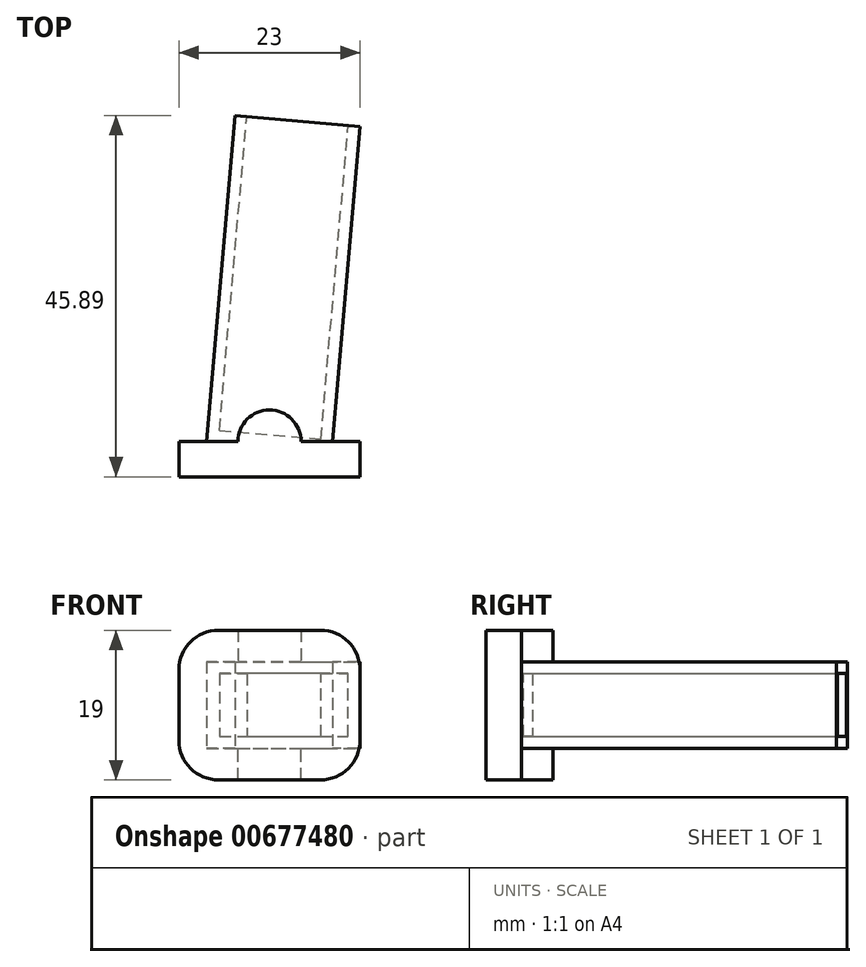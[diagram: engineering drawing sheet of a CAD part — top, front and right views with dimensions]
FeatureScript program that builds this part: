
annotation { "Feature Type Name" : "Feature", "Feature Type Description" : "" }
export const myFeature = defineFeature(function(context is Context, id is Id, definition is map)
    precondition{}
    {
        {
            var Q0;
            Q0=qCreatedBy(makeId("Top.planeOp"),FACE);
            var sketch = newSketch(context, id + "F0", { "sketchPlane" : qUnion([Q0])});
            skLineSegment(sketch, "E0", {"start": v(29.52, -9.85) * mm, "end": v(25.9, -51.24) * mm});
            skLineSegment(sketch, "E1", {"start": v(29.52, -9.85) * mm, "end": v(45.4, -11.24) * mm});
            skLineSegment(sketch, "E2", {"start": v(45.4, -11.24) * mm, "end": v(41.9, -51.24) * mm});
            skLineSegment(sketch, "E3", {"start": v(25.9, -51.24) * mm, "end": v(41.9, -51.24) * mm});
            skLineSegment(sketch, "E4", {"start": v(25.9, -51.24) * mm, "end": v(22.4, -51.24) * mm});
            skLineSegment(sketch, "E5", {"start": v(22.4, -51.24) * mm, "end": v(22.4, -55.74) * mm});
            skLineSegment(sketch, "E6", {"start": v(22.4, -55.74) * mm, "end": v(45.4, -55.74) * mm});
            skLineSegment(sketch, "E7", {"start": v(41.9, -51.24) * mm, "end": v(45.4, -51.24) * mm});
            skLineSegment(sketch, "E8", {"start": v(45.4, -51.24) * mm, "end": v(45.4, -55.74) * mm});
            skSolve(sketch);
        }
        {
            var Q0;
            {var subQ0=sQuery(id+"F0.wireOp",EDGE,"E2");Q0=makeQuery(id+"F0.imprint","IMPRINT",FACE,{"disambiguationData":[TD([[makeQuery(id+"F0.imprint","IMPRINT",EDGE,{"derivedFrom":subQ0}),-1.0]])]});}
            extrude(context, id + "F1", {"entities" : qUnion([Q0]), "endBound" : BoundingType.SYMMETRIC, "depth" : 11 * mm, "offsetDistance" : 25 * mm});
        }
        {
            var Q0;
            Q0=makeQuery(id+"F0.imprint","IMPRINT",FACE,{"disambiguationData":[TD([[makeQuery(id+"F0.imprint","IMPRINT",EDGE,{"derivedFrom":sQuery(id+"F0.wireOp",EDGE,"E3")}),-1.0]])]});
            var Q1;
            Q1=qSketchRegion(id+"F0e6qLEDJKoxhYJ_1",true);
            extrude(context, id + "F2", {"entities" : qUnion([Q0, Q1]), "operationType" : NewBodyOperationType.ADD, "endBound" : BoundingType.SYMMETRIC, "depth" : 19 * mm, "offsetDistance" : 25 * mm});
        }
        {
            var Q0;
            Q0=makeQuery(id+"F1.opExtrude","SWEPT_FACE",FACE,{"disambiguationData":[OSD([sQuery(id+"F0.wireOp",EDGE,"E1")])]});
            var sketch = newSketch(context, id + "F3", { "sketchPlane" : qUnion([Q0])});
            skLineSegment(sketch, "E9", {"start": v(-31.77, -4) * mm, "end": v(-44.7, -4) * mm});
            skLineSegment(sketch, "E10", {"start": v(-44.7, -4) * mm, "end": v(-44.7, 4) * mm});
            skLineSegment(sketch, "E11", {"start": v(-44.7, 4) * mm, "end": v(-31.77, 4) * mm});
            skLineSegment(sketch, "E12", {"start": v(-31.77, 4) * mm, "end": v(-31.77, -4) * mm});
            skSolve(sketch);
        }
        {
            var Q0;
            Q0=makeQuery(id+"F1.opExtrude","CAP_FACE",FACE,{"disambiguationData":[OSD([sQuery(id+"F0.wireOp",EDGE,"E0"),sQuery(id+"F0.wireOp",EDGE,"E1"),sQuery(id+"F0.wireOp",EDGE,"E2"),sQuery(id+"F0.wireOp",EDGE,"E3")])],"isStart":false});
            var sketch = newSketch(context, id + "F4", { "sketchPlane" : qUnion([Q0])});
            skCircle(sketch, "E13", {"center": v(33.9, -51.24) * mm, "radius": 4 * mm});
            skSolve(sketch);
        }
        {
            var Q0;
            {var subQ0=sQuery(id+"F4.wireOp",EDGE,"E13");var subQ1=makeQuery(id+"F1.opExtrude","CAP_EDGE",EDGE,{"disambiguationData":[OSD([sQuery(id+"F0.wireOp",EDGE,"E3")])],"isStart":false});var subQ2=makeQuery(id+"F4.imprint","INTERSECT",VERTEX,{"disambiguationData":[OD(0.0)],"derivedFrom":[subQ1,subQ0]});Q0=makeQuery(id+"F4.imprint","IMPRINT",FACE,{"disambiguationData":[TD([[makeQuery(id+"F4.imprint","IMPRINT",EDGE,{"disambiguationData":[TD([[subQ2,1.0]])],"derivedFrom":subQ0}),1.0]])]});}
            extrude(context, id + "F5", {"entities" : qUnion([Q0]), "operationType" : NewBodyOperationType.ADD, "depth" : 4 * mm, "offsetDistance" : 25 * mm});
        }
        {
            var Q0;
            Q0=makeQuery(id+"F1.opExtrude","CAP_FACE",FACE,{"disambiguationData":[OSD([sQuery(id+"F0.wireOp",EDGE,"E0"),sQuery(id+"F0.wireOp",EDGE,"E1"),sQuery(id+"F0.wireOp",EDGE,"E2"),sQuery(id+"F0.wireOp",EDGE,"E3")])],"isStart":true});
            var sketch = newSketch(context, id + "F6", { "sketchPlane" : qUnion([Q0])});
            skCircle(sketch, "E14", {"center": v(33.9, 51.24) * mm, "radius": 4 * mm});
            skSolve(sketch);
        }
        {
            var Q0;
            {var subQ0=sQuery(id+"F6.wireOp",EDGE,"E14");var subQ1=makeQuery(id+"F1.opExtrude","CAP_EDGE",EDGE,{"disambiguationData":[OSD([sQuery(id+"F0.wireOp",EDGE,"E3")])],"isStart":true});var subQ2=makeQuery(id+"F6.imprint","INTERSECT",VERTEX,{"disambiguationData":[OD(0.0)],"derivedFrom":[subQ1,subQ0]});Q0=makeQuery(id+"F6.imprint","IMPRINT",FACE,{"disambiguationData":[TD([[makeQuery(id+"F6.imprint","IMPRINT",EDGE,{"disambiguationData":[TD([[subQ2,-1.0]])],"derivedFrom":subQ0}),1.0]])]});}
            extrude(context, id + "F7", {"entities" : qUnion([Q0]), "operationType" : NewBodyOperationType.ADD, "depth" : 4 * mm, "offsetDistance" : 25 * mm});
        }
        {
            var Q0;
            Q0=makeQuery(id+"F2.opExtrude","CAP_EDGE",EDGE,{"disambiguationData":[OSD([sQuery(id+"F0.wireOp",EDGE,"E5")])],"isStart":false});
            fillet(context, id + "F8", {"entities" : qUnion([Q0]), "radius" : 5 * mm, "tangentPropagation" : true, "allowEdgeOverflow" : false});
        }
        {
            var Q0;
            Q0=makeQuery(id+"F2.opExtrude","CAP_EDGE",EDGE,{"disambiguationData":[OSD([sQuery(id+"F0.wireOp",EDGE,"E8")])],"isStart":false});
            fillet(context, id + "F9", {"entities" : qUnion([Q0]), "radius" : 5 * mm, "tangentPropagation" : true, "allowEdgeOverflow" : false});
        }
        {
            var Q0;
            Q0=makeQuery(id+"F2.opExtrude","CAP_EDGE",EDGE,{"disambiguationData":[OSD([sQuery(id+"F0.wireOp",EDGE,"E8")])],"isStart":true});
            fillet(context, id + "F10", {"entities" : qUnion([Q0]), "radius" : 5 * mm, "tangentPropagation" : true, "allowEdgeOverflow" : false});
        }
        {
            var Q0;
            Q0=makeQuery(id+"F2.opExtrude","CAP_EDGE",EDGE,{"disambiguationData":[OSD([sQuery(id+"F0.wireOp",EDGE,"E5")])],"isStart":true});
            fillet(context, id + "F11", {"entities" : qUnion([Q0]), "radius" : 5 * mm, "tangentPropagation" : true, "allowEdgeOverflow" : false});
        }
        {
            var Q0;
            Q0=makeQuery(id+"F3.imprint","IMPRINT",FACE,{"disambiguationData":[TD([[makeQuery(id+"F3.imprint","IMPRINT",EDGE,{"derivedFrom":sQuery(id+"F3.wireOp",EDGE,"E9")}),-1.0]])]});
            extrude(context, id + "F12", {"entities" : qUnion([Q0]), "operationType" : NewBodyOperationType.REMOVE, "oppositeDirection" : true, "depth" : 40 * mm, "offsetDistance" : 25 * mm});
        }
    });
